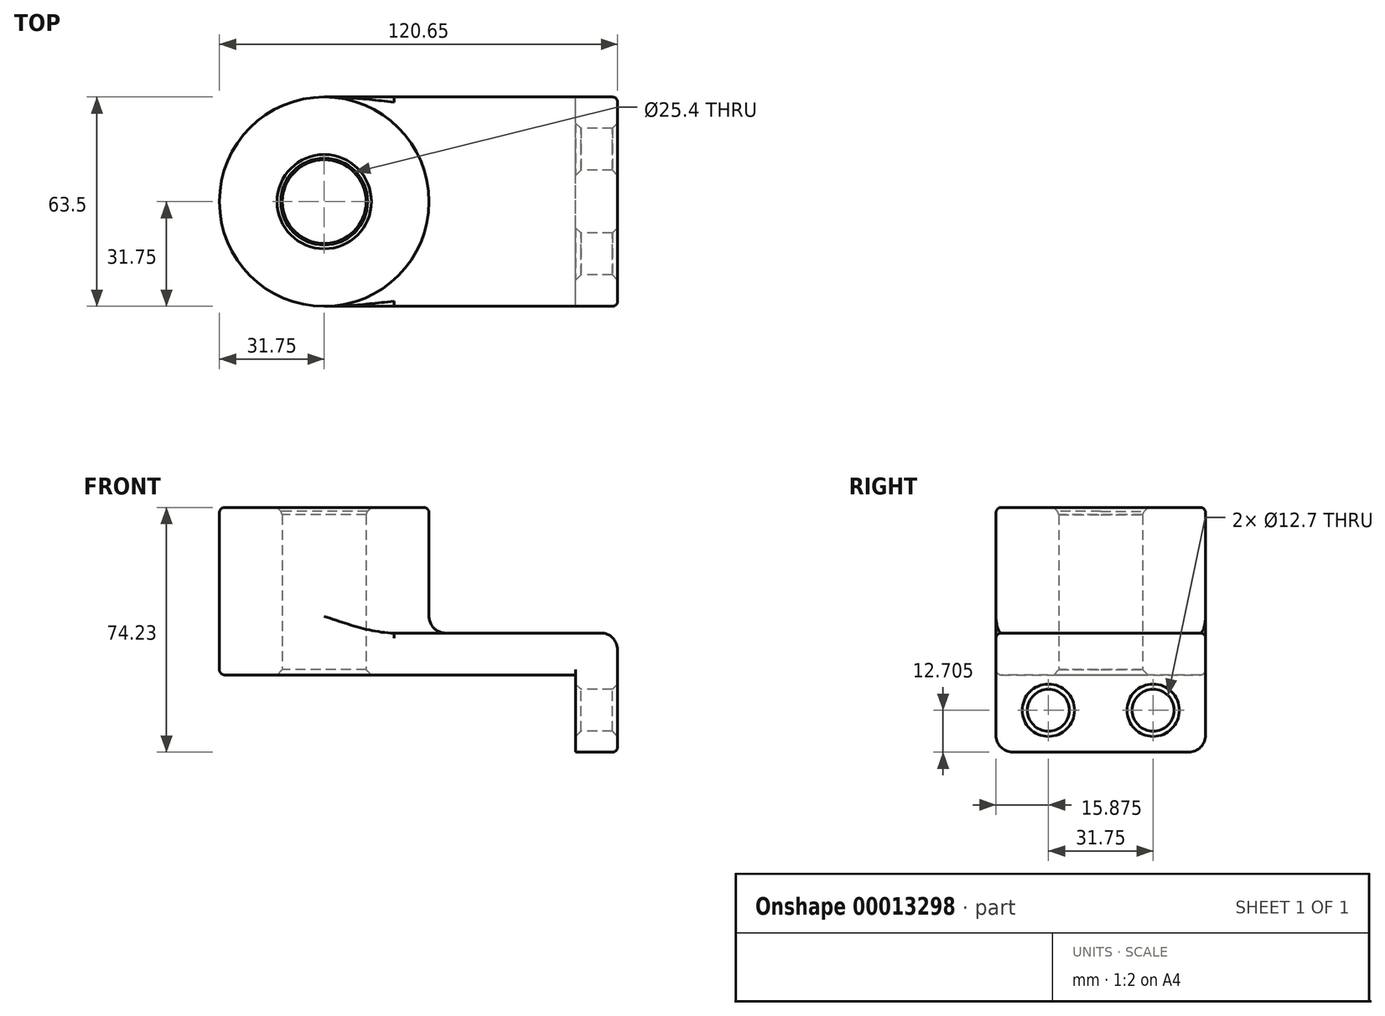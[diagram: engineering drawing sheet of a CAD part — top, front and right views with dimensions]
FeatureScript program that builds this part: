
annotation { "Feature Type Name" : "Feature", "Feature Type Description" : "" }
export const myFeature = defineFeature(function(context is Context, id is Id, definition is map)
    precondition{}
    {
        {
            var Q0;
            Q0=qCreatedBy(makeId("Top.planeOp"),FACE);
            var sketch = newSketch(context, id + "F0", { "sketchPlane" : qUnion([Q0])});
            skLineSegment(sketch, "E0.rect.bottom", {"start": v(38.1, -31.75) * mm, "end": v(-38.1, -31.75) * mm});
            skLineSegment(sketch, "E0.rect.top", {"start": v(38.1, 31.75) * mm, "end": v(-38.1, 31.75) * mm});
            skLineSegment(sketch, "E0.rect.left", {"start": v(38.1, -31.75) * mm, "end": v(38.1, 31.75) * mm});
            skLineSegment(sketch, "E0.rect.right", {"start": v(-38.1, -31.75) * mm, "end": v(-38.1, 31.75) * mm});
            skPoint(sketch, "E0.rect.middle", {"position": v(0, 0) * mm});
            skCircle(sketch, "E1", {"center": v(-38.1, 0) * mm, "radius": 31.75 * mm});
            skCircle(sketch, "E2", {"center": v(-38.1, 0) * mm, "radius": 12.7 * mm});
            skSolve(sketch);
        }
        {
            var Q0;
            {var subQ3=sQuery(id+"F0.wireOp",EDGE,"E0.rect.bottom");Q0=makeQuery(id+"F0.imprint","IMPRINT",FACE,{"disambiguationData":[TD([[makeQuery(id+"F0.imprint","IMPRINT",EDGE,{"derivedFrom":subQ3}),-1.0]])]});}
            var Q1;
            {var subQ0=sQuery(id+"F0.wireOp",EDGE,"E2");var subQ1=sQuery(id+"F0.wireOp",EDGE,"E0.rect.right");var subQ3=makeQuery(id+"F0.imprint","INTERSECT",VERTEX,{"disambiguationData":[OD(0.0)],"derivedFrom":[subQ1,subQ0]});Q1=makeQuery(id+"F0.imprint","IMPRINT",FACE,{"disambiguationData":[TD([[makeQuery(id+"F0.imprint","IMPRINT",EDGE,{"disambiguationData":[TD([[subQ3,-1.0]])],"derivedFrom":subQ0}),-1.0]])]});}
            var Q2;
            {var subQ0=sQuery(id+"F0.wireOp",EDGE,"E2");var subQ1=sQuery(id+"F0.wireOp",EDGE,"E0.rect.right");var subQ3=makeQuery(id+"F0.imprint","INTERSECT",VERTEX,{"disambiguationData":[OD(0.0)],"derivedFrom":[subQ1,subQ0]});Q2=makeQuery(id+"F0.imprint","IMPRINT",FACE,{"disambiguationData":[TD([[makeQuery(id+"F0.imprint","IMPRINT",EDGE,{"disambiguationData":[TD([[subQ3,1.0]])],"derivedFrom":subQ0}),-1.0]])]});}
            extrude(context, id + "F1", {"entities" : qUnion([Q0, Q1, Q2]), "depth" : 12.7 * mm});
        }
        {
            var Q0;
            {var subQ0=sQuery(id+"F0.wireOp",EDGE,"E2");var subQ1=sQuery(id+"F0.wireOp",EDGE,"E0.rect.right");var subQ3=makeQuery(id+"F0.imprint","INTERSECT",VERTEX,{"disambiguationData":[OD(0.0)],"derivedFrom":[subQ1,subQ0]});Q0=makeQuery(id+"F0.imprint","IMPRINT",FACE,{"disambiguationData":[TD([[makeQuery(id+"F0.imprint","IMPRINT",EDGE,{"disambiguationData":[TD([[subQ3,1.0]])],"derivedFrom":subQ0}),-1.0]])]});}
            var Q1;
            {var subQ0=sQuery(id+"F0.wireOp",EDGE,"E2");var subQ1=sQuery(id+"F0.wireOp",EDGE,"E0.rect.right");var subQ3=makeQuery(id+"F0.imprint","INTERSECT",VERTEX,{"disambiguationData":[OD(0.0)],"derivedFrom":[subQ1,subQ0]});Q1=makeQuery(id+"F0.imprint","IMPRINT",FACE,{"disambiguationData":[TD([[makeQuery(id+"F0.imprint","IMPRINT",EDGE,{"disambiguationData":[TD([[subQ3,-1.0]])],"derivedFrom":subQ0}),-1.0]])]});}
            extrude(context, id + "F2", {"entities" : qUnion([Q0, Q1]), "operationType" : NewBodyOperationType.ADD, "depth" : 50.8 * mm});
        }
        {
            var Q0;
            Q0=makeQuery(id+"F1.opExtrude","SWEPT_FACE",FACE,{"disambiguationData":[OSD([sQuery(id+"F0.wireOp",EDGE,"E0.rect.left")])]});
            var sketch = newSketch(context, id + "F3", { "sketchPlane" : qUnion([Q0])});
            skLineSegment(sketch, "E3.bottom", {"start": v(-31.75, 12.7) * mm, "end": v(31.75, 12.7) * mm});
            skLineSegment(sketch, "E3.top", {"start": v(-31.75, -23.43) * mm, "end": v(31.75, -23.43) * mm});
            skLineSegment(sketch, "E3.left", {"start": v(-31.75, 12.7) * mm, "end": v(-31.75, -23.43) * mm});
            skLineSegment(sketch, "E3.right", {"start": v(31.75, 12.7) * mm, "end": v(31.75, -23.43) * mm});
            skLineSegment(sketch, "E4", {"start": v(0, -23.43) * mm, "end": v(0, 0) * mm, "construction": true});
            skCircle(sketch, "E5", {"center": v(-15.88, -10.73) * mm, "radius": 6.35 * mm});
            skCircle(sketch, "E6.1.MirrorC", {"center": v(15.88, -10.73) * mm, "radius": 6.35 * mm});
            skSolve(sketch);
        }
        {
            var Q0;
            {var subQ2=sQuery(id+"F3.wireOp",EDGE,"E3.bottom");Q0=makeQuery(id+"F3.imprint","IMPRINT",FACE,{"disambiguationData":[TD([[makeQuery(id+"F3.imprint","IMPRINT",EDGE,{"derivedFrom":subQ2}),-1.0]])]});}
            var Q1;
            {var subQ2=sQuery(id+"F3.wireOp",EDGE,"E3.top");Q1=makeQuery(id+"F3.imprint","IMPRINT",FACE,{"disambiguationData":[TD([[makeQuery(id+"F3.imprint","IMPRINT",EDGE,{"derivedFrom":subQ2}),1.0]])]});}
            extrude(context, id + "F4", {"entities" : qUnion([Q0, Q1]), "operationType" : NewBodyOperationType.ADD, "depth" : 12.7 * mm});
        }
        {
            var Q0;
            {var subQ0=sQuery(id+"F0.wireOp",EDGE,"E1");Q0=makeQuery(id+"F2.boolean.opBoolean","INTERSECT",EDGE,{"derivedFrom":[makeQuery(id+"F1.opExtrude","CAP_FACE",FACE,{"disambiguationData":[OSD([sQuery(id+"F0.wireOp",EDGE,"E0.rect.bottom"),sQuery(id+"F0.wireOp",EDGE,"E0.rect.top"),sQuery(id+"F0.wireOp",EDGE,"E0.rect.left"),subQ0,sQuery(id+"F0.wireOp",EDGE,"E2")])],"isStart":false}),makeQuery(id+"F2.opExtrude","SWEPT_FACE",FACE,{"disambiguationData":[OSD([subQ0])]})]});}
            var Q1;
            Q1=makeQuery(id+"F4.opExtrude","SWEPT_EDGE",EDGE,{"disambiguationData":[OSD([sQuery(id+"F3.wireOp",EDGE,"E3.top"),sQuery(id+"F3.wireOp",EDGE,"E3.left")])]});
            var Q2;
            Q2=makeQuery(id+"F4.opExtrude","SWEPT_EDGE",EDGE,{"disambiguationData":[OSD([sQuery(id+"F3.wireOp",EDGE,"E3.top"),sQuery(id+"F3.wireOp",EDGE,"E3.right")])]});
            var Q3;
            Q3=makeQuery(id+"F4.opExtrude","CAP_EDGE",EDGE,{"disambiguationData":[OSD([sQuery(id+"F3.wireOp",EDGE,"E3.bottom")])],"isStart":false});
            fillet(context, id + "F5", {"entities" : qUnion([Q0, Q1, Q2, Q3]), "radius" : 5.08 * mm, "tangentPropagation" : true, "allowEdgeOverflow" : false});
        }
        {
            var Q0;
            Q0=makeQuery(id+"F1.opExtrude","CAP_EDGE",EDGE,{"disambiguationData":[OSD([sQuery(id+"F0.wireOp",EDGE,"E0.rect.bottom")])],"isStart":true});
            var Q1;
            Q1=makeQuery(id+"F4.boolean.opBoolean","MERGE",EDGE,{"derivedFrom":[makeQuery(id+"F1.opExtrude","CAP_EDGE",EDGE,{"disambiguationData":[OSD([sQuery(id+"F0.wireOp",EDGE,"E0.rect.bottom")])],"isStart":false}),makeQuery(id+"F4.opExtrude","SWEPT_EDGE",EDGE,{"disambiguationData":[OSD([sQuery(id+"F3.wireOp",EDGE,"E3.bottom"),sQuery(id+"F3.wireOp",EDGE,"E3.left")])]})]});
            var Q2;
            Q2=makeQuery(id+"F2.opExtrude","CAP_EDGE",EDGE,{"disambiguationData":[OSD([sQuery(id+"F0.wireOp",EDGE,"E1")])],"isStart":false});
            fillet(context, id + "F6", {"entities" : qUnion([Q0, Q1, Q2]), "radius" : 1.59 * mm, "tangentPropagation" : true, "allowEdgeOverflow" : false});
        }
        {
            var Q0;
            Q0=makeQuery(id+"F2.opExtrude","CAP_EDGE",EDGE,{"disambiguationData":[OSD([sQuery(id+"F0.wireOp",EDGE,"E2")])],"isStart":false});
            chamfer(context, id + "F7", {"entities" : qUnion([Q0]), "width" : 1.59 * mm, "tangentPropagation" : true});
        }
        {
            var Q0;
            {var subQ0=sQuery(id+"F0.wireOp",EDGE,"E2");Q0=makeQuery(id+"F2.boolean.opBoolean","MERGE",FACE,{"derivedFrom":[makeQuery(id+"F1.opExtrude","SWEPT_FACE",FACE,{"disambiguationData":[OSD([subQ0])]}),makeQuery(id+"F2.opExtrude","SWEPT_FACE",FACE,{"disambiguationData":[OSD([subQ0])]})]});}
            var Q1;
            Q1=makeQuery(id+"F4.opExtrude","CAP_EDGE",EDGE,{"disambiguationData":[OSD([sQuery(id+"F3.wireOp",EDGE,"E5")])],"isStart":false});
            var Q2;
            Q2=makeQuery(id+"F4.opExtrude","CAP_EDGE",EDGE,{"disambiguationData":[OSD([sQuery(id+"F3.wireOp",EDGE,"E6.1.MirrorC")])],"isStart":false});
            var Q3;
            Q3=makeQuery(id+"F4.opExtrude","CAP_EDGE",EDGE,{"disambiguationData":[OSD([sQuery(id+"F3.wireOp",EDGE,"E5")])],"isStart":true});
            var Q4;
            Q4=makeQuery(id+"F4.opExtrude","CAP_EDGE",EDGE,{"disambiguationData":[OSD([sQuery(id+"F3.wireOp",EDGE,"E6.1.MirrorC")])],"isStart":true});
            chamfer(context, id + "F8", {"entities" : qUnion([Q0, Q1, Q2, Q3, Q4]), "width" : 1.59 * mm, "tangentPropagation" : true});
        }
    });
